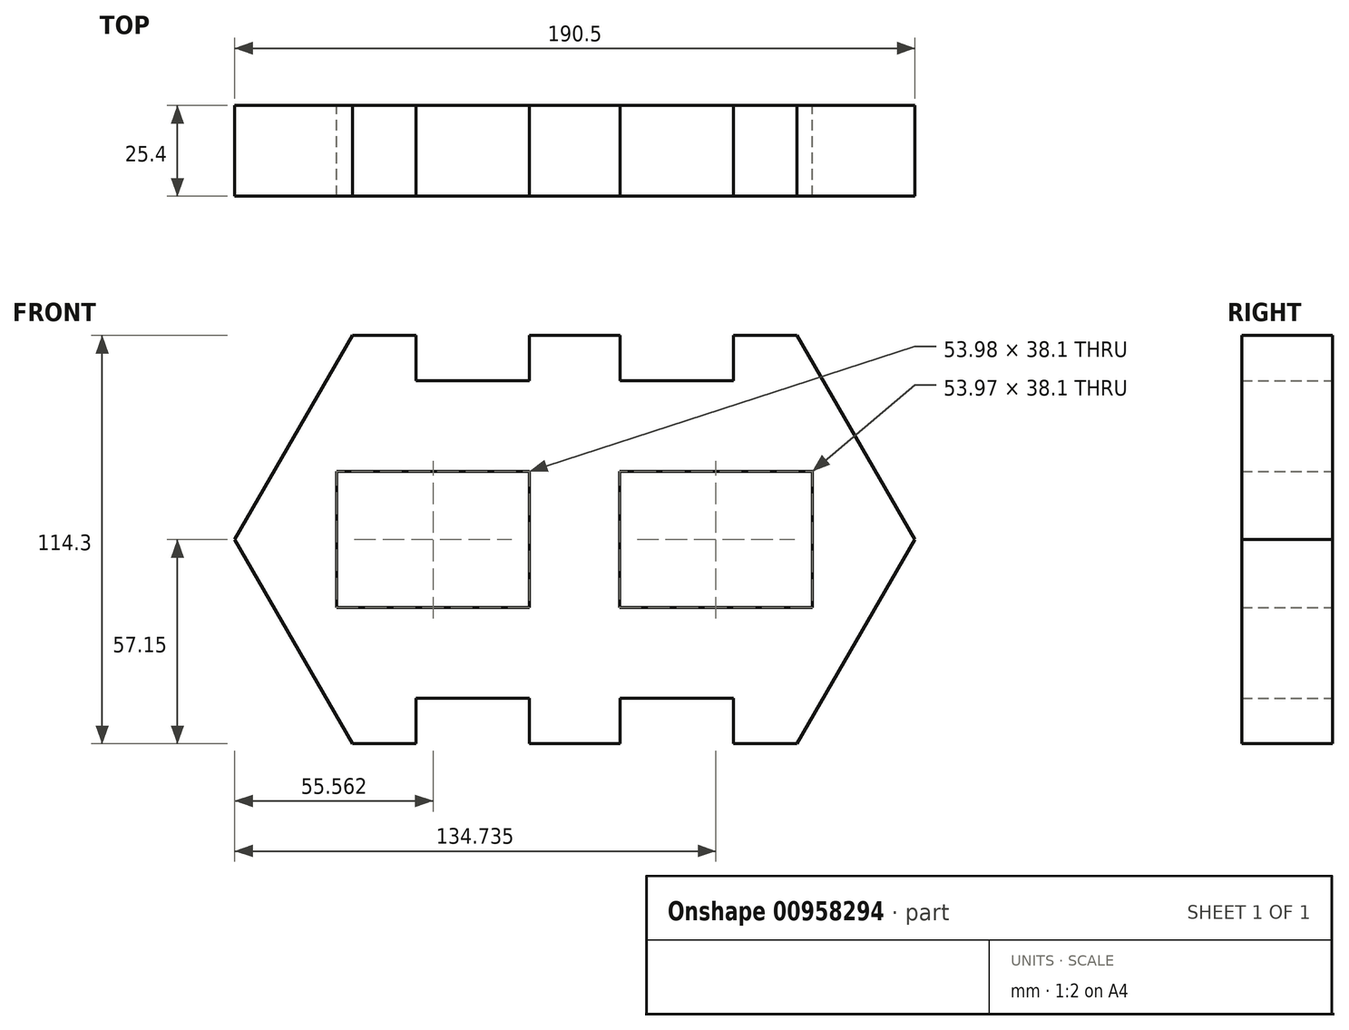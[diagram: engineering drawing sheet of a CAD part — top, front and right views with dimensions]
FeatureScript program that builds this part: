
annotation { "Feature Type Name" : "Feature", "Feature Type Description" : "" }
export const myFeature = defineFeature(function(context is Context, id is Id, definition is map)
    precondition{}
    {
        {
            var Q0;
            Q0=qCreatedBy(makeId("Front.planeOp"),FACE);
            var sketch = newSketch(context, id + "F0", { "sketchPlane" : qUnion([Q0])});
            skLineSegment(sketch, "E0.bottom", {"start": v(-49.55, 101.6) * mm, "end": v(-31.75, 101.6) * mm});
            skLineSegment(sketch, "E0.top", {"start": v(-49.55, -12.7) * mm, "end": v(-31.75, -12.7) * mm});
            skLineSegment(sketch, "E1", {"start": v(-49.55, 101.6) * mm, "end": v(-82.55, 44.45) * mm});
            skLineSegment(sketch, "E2", {"start": v(-82.55, 44.45) * mm, "end": v(-49.55, -12.7) * mm});
            skLineSegment(sketch, "E3", {"start": v(107.95, 44.45) * mm, "end": v(74.95, 101.6) * mm});
            skLineSegment(sketch, "E4", {"start": v(107.95, 44.45) * mm, "end": v(74.95, -12.7) * mm});
            skLineSegment(sketch, "E5", {"start": v(74.95, 101.6) * mm, "end": v(57.15, 101.6) * mm});
            skLineSegment(sketch, "E6", {"start": v(-31.75, 101.6) * mm, "end": v(-31.75, 88.9) * mm});
            skLineSegment(sketch, "E7", {"start": v(-31.75, 88.9) * mm, "end": v(0, 88.9) * mm});
            skLineSegment(sketch, "E8", {"start": v(0, 88.9) * mm, "end": v(0, 101.6) * mm});
            skLineSegment(sketch, "E9", {"start": v(0, 101.6) * mm, "end": v(25.4, 101.6) * mm});
            skLineSegment(sketch, "E10", {"start": v(25.4, 101.6) * mm, "end": v(25.4, 88.9) * mm});
            skLineSegment(sketch, "E11", {"start": v(25.4, 88.9) * mm, "end": v(57.15, 88.9) * mm});
            skLineSegment(sketch, "E12", {"start": v(57.15, 88.9) * mm, "end": v(57.15, 101.6) * mm});
            skLineSegment(sketch, "E13", {"start": v(-31.75, 0) * mm, "end": v(-31.75, -12.7) * mm});
            skLineSegment(sketch, "E14", {"start": v(-31.75, -12.7) * mm, "end": v(-31.75, 0) * mm});
            skLineSegment(sketch, "E15", {"start": v(-31.75, 0) * mm, "end": v(0, 0) * mm});
            skLineSegment(sketch, "E16", {"start": v(0, 0) * mm, "end": v(0, -12.7) * mm});
            skPoint(sketch, "E16.endSnap0", {"position": v(12.7, -12.7) * mm});
            skLineSegment(sketch, "E17", {"start": v(25.4, 0) * mm, "end": v(25.4, -12.7) * mm});
            skLineSegment(sketch, "E18", {"start": v(25.4, 0) * mm, "end": v(57.15, 0) * mm});
            skLineSegment(sketch, "E19", {"start": v(57.15, 0) * mm, "end": v(57.15, -12.7) * mm});
            skLineSegment(sketch, "E20.bottom", {"start": v(-53.98, 63.5) * mm, "end": v(0, 63.5) * mm});
            skLineSegment(sketch, "E20.top", {"start": v(-53.98, 25.4) * mm, "end": v(0, 25.4) * mm});
            skLineSegment(sketch, "E20.left", {"start": v(-53.98, 63.5) * mm, "end": v(-53.98, 25.4) * mm});
            skLineSegment(sketch, "E20.right", {"start": v(0, 63.5) * mm, "end": v(0, 25.4) * mm});
            skLineSegment(sketch, "E21.bottom", {"start": v(79.17, 63.5) * mm, "end": v(25.2, 63.5) * mm});
            skLineSegment(sketch, "E21.top", {"start": v(79.17, 25.4) * mm, "end": v(25.2, 25.4) * mm});
            skLineSegment(sketch, "E21.left", {"start": v(79.17, 63.5) * mm, "end": v(79.17, 25.4) * mm});
            skLineSegment(sketch, "E21.right", {"start": v(25.2, 63.5) * mm, "end": v(25.2, 25.4) * mm});
            skLineSegment(sketch, "E22.trimOffspring", {"start": v(57.15, 101.6) * mm, "end": v(74.95, 101.6) * mm});
            skLineSegment(sketch, "E23.trimOffspring", {"start": v(57.15, -12.7) * mm, "end": v(74.95, -12.7) * mm});
            skLineSegment(sketch, "E24.trimOffspring", {"start": v(0, -12.7) * mm, "end": v(25.4, -12.7) * mm});
            skSolve(sketch);
        }
        {
            var Q0;
            Q0 = qSketchRegion(id + "F0", true);
            extrude(context, id + "F1", {"entities" : qUnion([Q0]), "depth" : 25.4 * mm, "offsetDistance" : 25.4 * mm});
        }
    });
